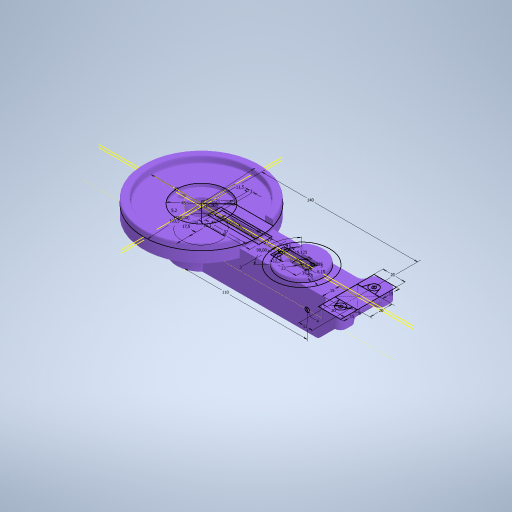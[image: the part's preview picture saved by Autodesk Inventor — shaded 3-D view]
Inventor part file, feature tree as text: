
AUTODESK INVENTOR PART (.ipt)
format: ipt  version: 2024.2 (Build 282272000, 272)  size: 731,648 bytes
history: native  units: mm
features: extrude x17, other x7, fillet x7, sketch x6, chamfer x1
ambient origin geometry x8: Origin, YZ Plane, XZ Plane, XY Plane, X Axis, Y Axis, Z Axis, Center Point
bodies: Body1 (feature_tree)
feature tree (38):
  other  "Bryła1"
  sketch  "Szkic1"
  extrude  "Wyciągnięcie proste3"  Depth=22.1mm
  extrude  "Wyciągnięcie proste1"  Depth=44.0mm
  extrude  "Wyciągnięcie proste2"  Depth=20.0mm TaperAngle=0.0deg
  sketch  "Szkic4"
  extrude  "Wyciągnięcie proste5"  Depth=17.5mm
  extrude  "Wyciągnięcie proste6"  Depth=5.2mm
  extrude  "Wyciągnięcie proste7"  Depth=30.0mm TaperAngle=360.0deg
  extrude  "Wyciągnięcie proste9"  TaperAngle=0.0deg  [1 undecoded]
  fillet  "Zaokrąglenie1"  Radius=35.0mm
  fillet  "Zaokrąglenie2"  Radius=30.0mm
  sketch  "Szkic6"
  extrude  "Wyciągnięcie proste10"  Depth=150.0mm TaperAngle=0.0deg
  extrude  "Wyciągnięcie proste11"  Depth=17.5mm TaperAngle=0.0deg
  extrude  "Wyciągnięcie proste4"  Depth=40.0mm TaperAngle=0.0deg
  fillet  "Zaokrąglenie4"  Radius=90.0mm
  fillet  "Zaokrąglenie5"  Radius=12.3mm
  extrude  "Wyciągnięcie proste12"  TaperAngle=0.0deg  [1 undecoded]
  extrude  "Wyciągnięcie proste13"  Depth=23.0mm
  extrude  "Wyciągnięcie proste14"  Depth=12.3mm
  chamfer  "Faza1"  Distance=6.15mm
  fillet  "Zaokrąglenie6"  Radius=8.375mm
  sketch  "Szkic7"
  extrude  "Wyciągnięcie proste19"  Depth=19.125mm
  extrude  "Wyciągnięcie proste20"  Depth=5.0mm
  fillet  "Zaokrąglenie9"  Radius=5.0mm
  extrude  "Wyciągnięcie proste21"  Depth=3.0mm
  extrude  "Wyciągnięcie proste18"  Depth=3.0mm
  fillet  "Zaokrąglenie10"  Radius=6.0mm
  sketch  "Szkic11"
  sketch  "Szkic2"
  other  "Finish1"
  other  "Finish2"
  other  "Finish3"
  other  "Finish4"
  other  "Finish5"
  other  "Finish6"
note: 2 required parameter values undecoded (feature->parameter linkage not recoverable at this tier; creation-order binding heuristic only, values carry confidence <= 0.55)
